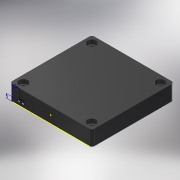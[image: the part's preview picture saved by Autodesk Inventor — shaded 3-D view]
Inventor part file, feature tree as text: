
AUTODESK INVENTOR PART (.ipt)
format: ipt  version: 2017 (Build 210142000, 142)  size: 156,160 bytes
history: native  units: mm
features: sketch x3, extrude x1, hole x1, fillet x1
ambient origin geometry x8: Origin, YZ Plane, XZ Plane, XY Plane, X Axis, Y Axis, Z Axis, Center Point
bodies: Solide1 (feature_tree)
feature tree (6):
  extrude  "Extrusion1"  Depth=60.0mm
  hole  "Perçage1"  [1 undecoded]
  fillet  "Congé1"  Radius=11.0mm
  sketch  "Esquisse3"
  sketch  "Esquisse1"
  sketch  "Esquisse2"
note: 1 required parameter value undecoded (feature->parameter linkage not recoverable at this tier; creation-order binding heuristic only, values carry confidence <= 0.55)
